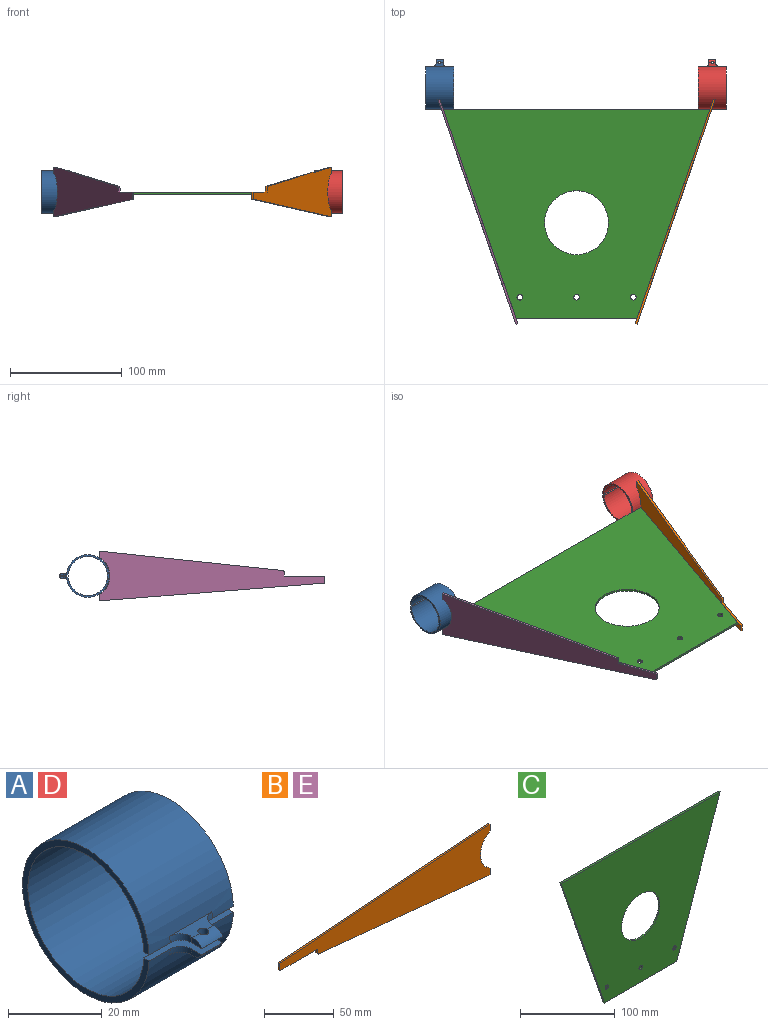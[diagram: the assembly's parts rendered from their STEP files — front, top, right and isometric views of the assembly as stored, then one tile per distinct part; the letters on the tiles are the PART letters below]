
ASSEMBLY  parts=5 mates=5
PART A: 20 faces, bbox 25.4x44.5x38.1 mm
  f0: cylinder r=3.17mm len=6.35mm, axis (1,0,0), area 19mm2, adj f5,f11,f12,f13,f19
  f1: cylinder r=3.17mm len=6.35mm, axis (-1,0,0), area 19mm2, adj f3,f8,f9,f10,f18
  f2: cylinder r=19.05mm len=38.1mm, axis (-1,0,0), area 2959.4mm2, adj f3,f5,f6,f7,f8,f11,f14,f15
  f3: plane 25.4x7.96mm, normal (0,0,-1), area 81mm2, adj f1,f2,f4,f6,f7,f9,f10,f16
  f4: cylinder r=17.46mm len=34.93mm, axis (-1,0,0), area 2746.6mm2, adj f3,f5,f6,f7
  f5: plane 25.4x7.96mm, normal (0,0,1), area 81mm2, adj f0,f2,f4,f6,f7,f12,f13,f14
  f6: plane 38.1x38.08mm, normal (1,0,0), area 179.6mm2, adj f2,f3,f4,f5
  f7: plane 38.1x38.08mm, normal (-1,0,0), area 179.6mm2, adj f2,f3,f4,f5
  f8: plane 12.7x3.75mm, normal (0,0,1), area 26.1mm2, adj f1,f2,f9,f10,f16,f17,f18
  f9: plane 3.3x1.59mm, normal (1,0,0), area 3.9mm2, adj f1,f3,f8,f16
  f10: plane 3.3x1.59mm, normal (-1,0,0), area 3.9mm2, adj f1,f3,f8,f17
  f11: plane 12.7x3.75mm, normal (0,0,-1), area 26.1mm2, adj f0,f2,f12,f13,f14,f15,f19
  f12: plane 3.3x1.59mm, normal (1,0,0), area 3.9mm2, adj f0,f5,f11,f14
  f13: plane 3.3x1.59mm, normal (-1,0,0), area 3.9mm2, adj f0,f5,f11,f15
  f14: torus R=22.23mm, axis (1,0,0), area 7.9mm2, adj f2,f5,f11,f12
  f15: torus R=22.23mm, axis (1,0,0), area 7.9mm2, adj f2,f5,f11,f13
  f16: torus R=22.23mm, axis (1,0,0), area 7.9mm2, adj f2,f3,f8,f9
  f17: torus R=22.23mm, axis (1,0,0), area 7.9mm2, adj f2,f3,f8,f10
  f18: cylinder r=1.14mm len=2.29mm, axis (0,0,-1), area 11mm2, adj f1,f3,f8
  f19: cylinder r=1.14mm len=2.29mm, axis (0,0,-1), area 11mm2, adj f0,f5,f11
PART B: 11 faces, bbox 212.7x1.9x44.5 mm
  f0: plane 173.2x17.32mm, normal (-0.1,0,-1), area 322.7mm2, adj f1,f8,f9,f10
  f1: plane 5.73x1.85mm, normal (1,0,0), area 10.6mm2, adj f0,f2,f9,f10
  f2: cylinder r=19.05mm len=33mm, axis (0,1,0), area 74mm2, adj f1,f3,f9,f10
  f3: plane 5.73x1.85mm, normal (1,0,0), area 10.6mm2, adj f2,f4,f9,f10
  f4: plane 212.73x15.88mm, normal (-0.07,0,1), area 395.5mm2, adj f3,f5,f9,f10
  f5: plane 6.35x1.85mm, normal (-1,0,0), area 11.8mm2, adj f4,f6,f9,f10
  f6: plane 38.1x1.85mm, normal (0,0,-1), area 70.6mm2, adj f5,f7,f9,f10
  f7: plane 3.33x1.85mm, normal (-1,0,0), area 6.2mm2, adj f6,f8,f9,f10
  f8: cylinder r=1.59mm len=1.85mm, axis (0,1,0), area 4.3mm2, adj f0,f7,f9,f10
  f9: plane 212.73x44.45mm, normal (0,-1,0), area 5172.3mm2, adj f0,f1,f2,f3,f4,f5,f6,f7
  f10: plane 212.73x44.45mm, normal (0,1,0), area 5172.3mm2, adj f0,f1,f2,f3,f4,f5,f6,f7
PART C: 10 faces, bbox 238.1x1.9x187.3 mm
  f0: plane 107.95x1.85mm, normal (0,0,-1), area 200.2mm2, adj f1,f6,f8,f9
  f1: plane 187.33x65.09mm, normal (0.94,0,-0.33), area 367.7mm2, adj f0,f2,f8,f9
  f2: plane 238.13x1.85mm, normal (0,0,1), area 441.5mm2, adj f1,f6,f8,f9
  f3: cylinder r=2.46mm len=4.92mm, axis (0,1,0), area 28.6mm2, adj f8,f9
  f4: cylinder r=2.46mm len=4.92mm, axis (0,1,0), area 28.6mm2, adj f8,f9
  f5: cylinder r=28.57mm len=57.15mm, axis (0,1,0), area 332.9mm2, adj f8,f9
  f6: plane 187.33x65.09mm, normal (-0.94,0,-0.33), area 367.7mm2, adj f0,f2,f8,f9
  f7: cylinder r=2.46mm len=4.92mm, axis (0,1,0), area 28.6mm2, adj f8,f9
  f8: plane 238.13x187.33mm, normal (0,-1,0), area 29792.1mm2, adj f0,f1,f2,f3,f4,f5,f6,f7
  f9: plane 238.13x187.33mm, normal (0,1,0), area 29792.1mm2, adj f0,f1,f2,f3,f4,f5,f6,f7
PART D: same geometry as A
PART E: same geometry as B
PLACE A rot(axis=(0,0,-1),180deg) t=(-122.29,120.59,0)mm
PLACE B rot(axis=(-0.81,-0.58,0),180deg) t=(127.04,118.92,0)mm
PLACE C rot(axis=(-1,0,0),90deg) t=(0,0,-1.85)mm
PLACE D rot(axis=(0,0,-1),180deg) t=(121.3,120.59,0)mm
PLACE E rot(axis=(0.58,0.81,0),180deg) t=(-125.29,119.53,0)mm
MATE cylindrical A.f4 <-> D.f4  axis (1,0,0) through (-109.59,120.59,0)mm
MATE planar E.f10 <-> C.f6  axis (0.94,0.33,0) through (-95.27,33.13,-1.13)mm
MATE planar C.f7 <-> B.f6  axis (0,0,1) through (50.8,-66.68,0)mm
MATE planar C.f8 <-> E.f6  axis (0,0,1) through (0,21.54,0)mm
MATE planar B.f9 <-> C.f1  axis (-0.94,0.33,0) through (95.27,33.13,-1.13)mm
